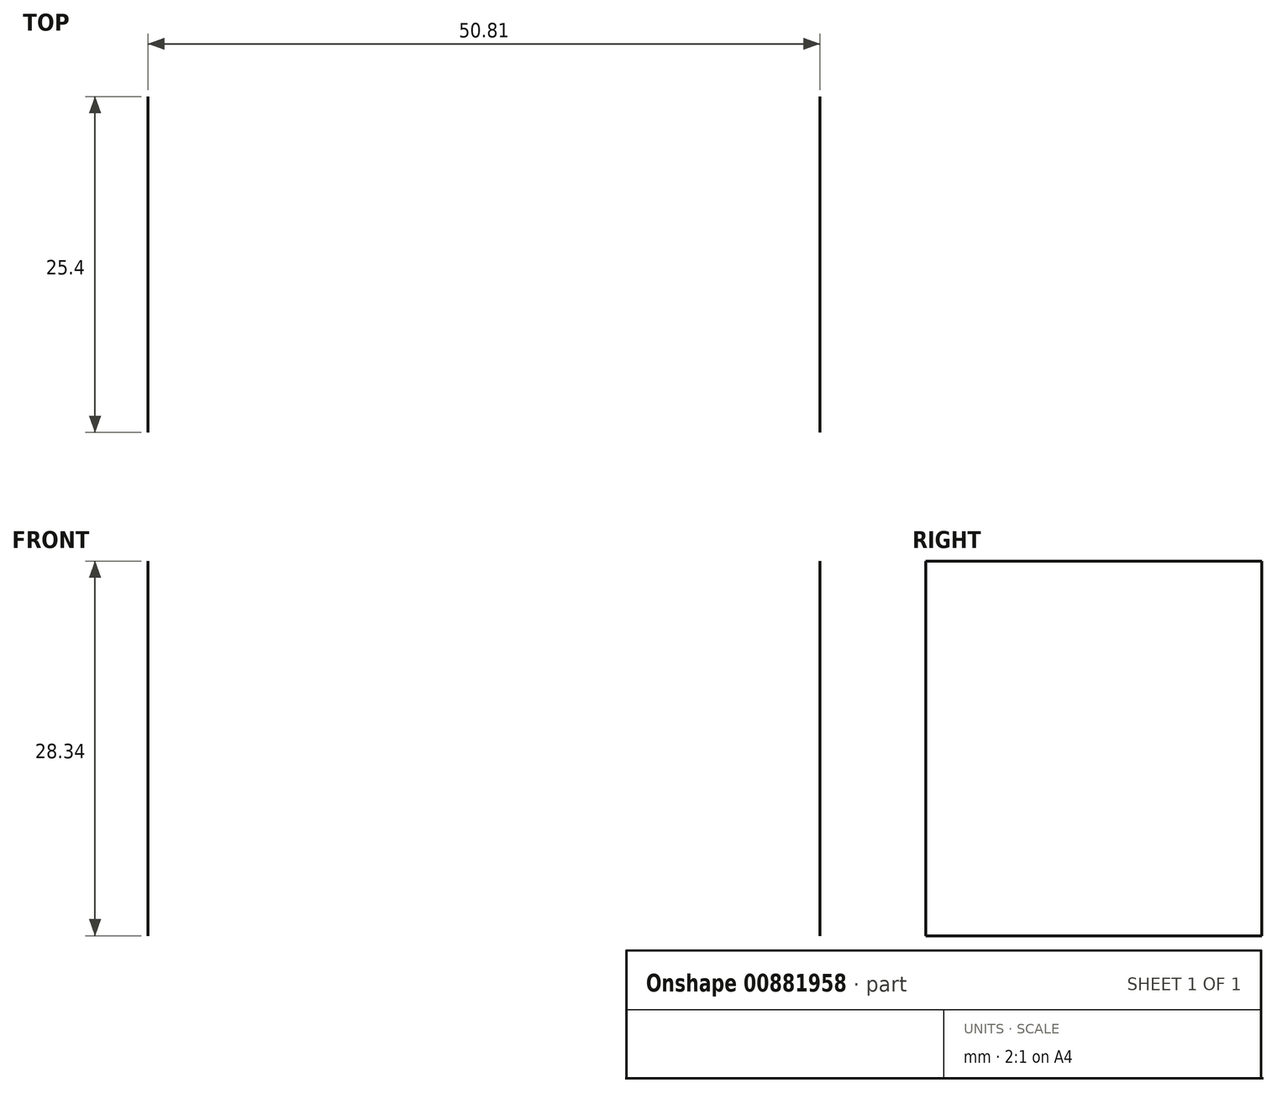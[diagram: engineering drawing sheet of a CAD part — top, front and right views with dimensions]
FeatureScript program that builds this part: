
annotation { "Feature Type Name" : "Feature", "Feature Type Description" : "" }
export const myFeature = defineFeature(function(context is Context, id is Id, definition is map)
    precondition{}
    {
        {
            var Q0;
            Q0=qCreatedBy(makeId("Front.planeOp"),FACE);
            var sketch = newSketch(context, id + "F0", { "sketchPlane" : qUnion([Q0])});
            skLineSegment(sketch, "E0.bottom", {"start": v(-34.03, 28.34) * mm, "end": v(16.78, 28.34) * mm});
            skLineSegment(sketch, "E0.top", {"start": v(-34.03, 0) * mm, "end": v(16.78, 0) * mm});
            skLineSegment(sketch, "E0.left", {"start": v(-34.03, 28.34) * mm, "end": v(-34.03, 0) * mm});
            skLineSegment(sketch, "E0.right", {"start": v(16.78, 28.34) * mm, "end": v(16.78, 0) * mm});
            skSolve(sketch);
        }
        {
            var Q0;
            Q0=sQuery(id+"F0.wireOp",EDGE,"E0.right");
            var Q1;
            Q1=sQuery(id+"F0.wireOp",EDGE,"E0.left");
            extrude(context, id + "F1", {"bodyType" : ToolBodyType.SURFACE, "surfaceEntities" : qUnion([Q0, Q1]), "depth" : 25.4 * mm, "offsetDistance" : 25.4 * mm});
        }
    });
